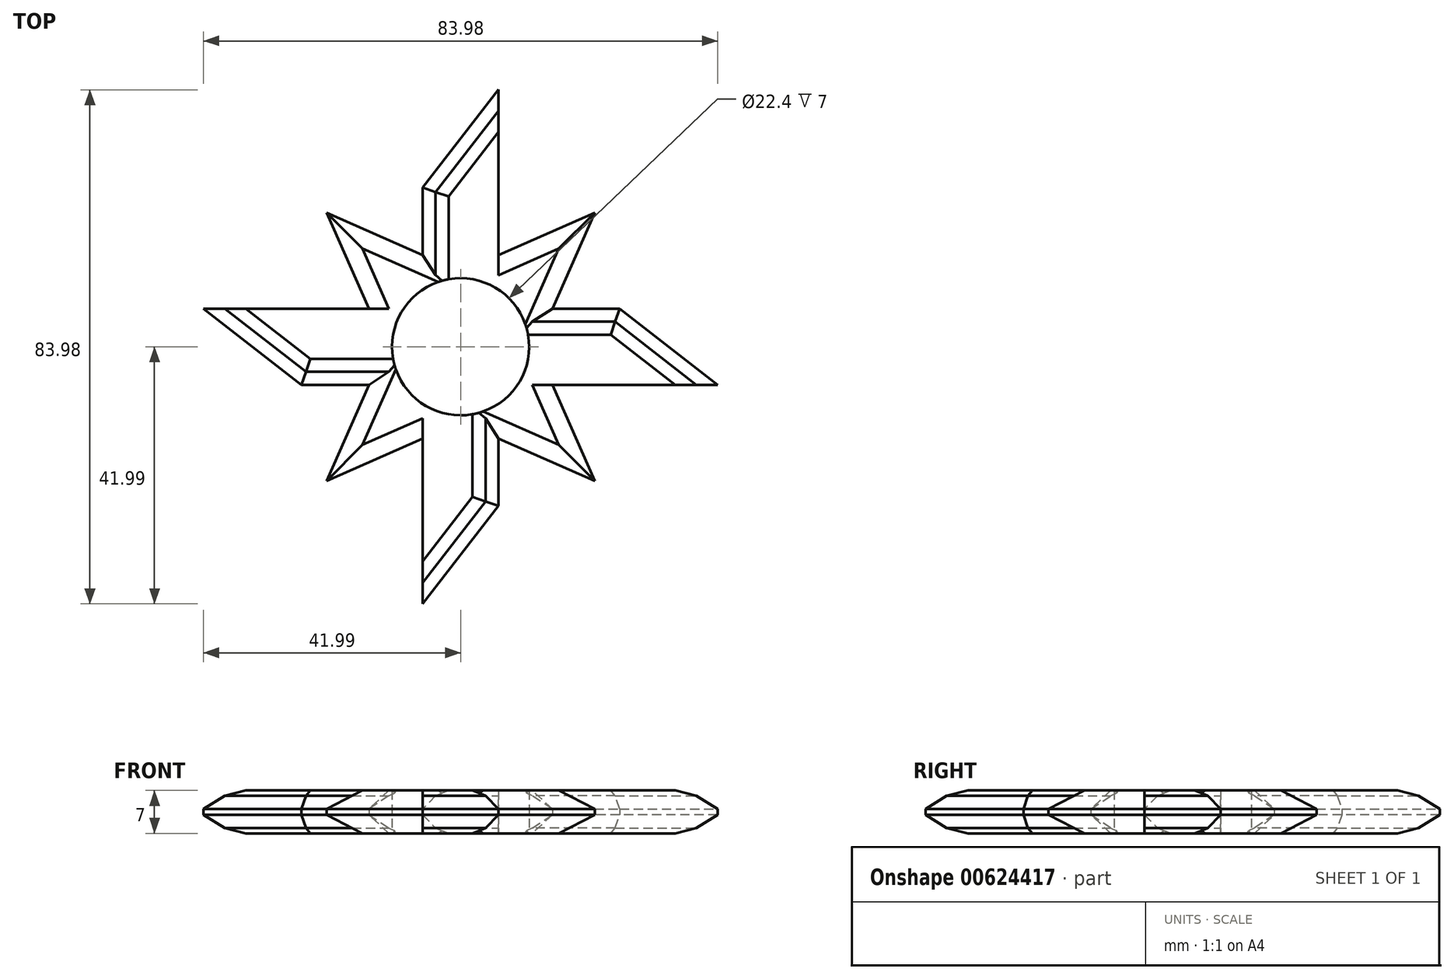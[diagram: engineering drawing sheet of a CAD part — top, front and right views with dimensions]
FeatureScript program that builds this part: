
annotation { "Feature Type Name" : "Feature", "Feature Type Description" : "" }
export const myFeature = defineFeature(function(context is Context, id is Id, definition is map)
    precondition{}
    {
        {
            var Q0;
            Q0=qCreatedBy(makeId("Top.planeOp"),FACE);
            var sketch = newSketch(context, id + "F0", { "sketchPlane" : qUnion([Q0])});
            skCircle(sketch, "E0", {"center": v(0, 0) * mm, "radius": 11.2 * mm});
            skCircle(sketch, "E1.cCircle", {"center": v(0, 0) * mm, "radius": 14.98 * mm, "construction": true});
            skLineSegment(sketch, "E1.0", {"start": v(14.98, 6.2) * mm, "end": v(14.98, -6.2) * mm});
            skLineSegment(sketch, "E1.1", {"start": v(14.98, -6.2) * mm, "end": v(6.2, -14.98) * mm});
            skLineSegment(sketch, "E1.2", {"start": v(6.2, -14.98) * mm, "end": v(-6.2, -14.98) * mm});
            skLineSegment(sketch, "E1.3", {"start": v(-6.2, -14.98) * mm, "end": v(-14.98, -6.2) * mm});
            skLineSegment(sketch, "E1.4", {"start": v(-14.98, -6.2) * mm, "end": v(-14.98, 6.2) * mm});
            skLineSegment(sketch, "E1.5", {"start": v(-14.98, 6.2) * mm, "end": v(-6.2, 14.98) * mm});
            skLineSegment(sketch, "E1.6", {"start": v(-6.2, 14.98) * mm, "end": v(6.2, 14.98) * mm});
            skLineSegment(sketch, "E1.7", {"start": v(6.2, 14.98) * mm, "end": v(14.98, 6.2) * mm});
            skPoint(sketch, "E1.0.midPoint", {"position": v(14.98, 0) * mm});
            skLineSegment(sketch, "E2", {"start": v(-14.98, 6.2) * mm, "end": v(-26, 6.2) * mm});
            skLineSegment(sketch, "E3", {"start": v(-26, 6.2) * mm, "end": v(-14.98, -6.2) * mm});
            skLineSegment(sketch, "E4", {"start": v(-14.98, -6.2) * mm, "end": v(-26, -6.2) * mm});
            skLineSegment(sketch, "E5", {"start": v(-26, -6.2) * mm, "end": v(-26, 6.2) * mm});
            skLineSegment(sketch, "E6", {"start": v(6.2, 14.98) * mm, "end": v(6.2, 26) * mm});
            skLineSegment(sketch, "E7", {"start": v(6.2, 26) * mm, "end": v(-6.2, 14.98) * mm});
            skLineSegment(sketch, "E8", {"start": v(-6.2, 14.98) * mm, "end": v(-6.2, 26) * mm});
            skLineSegment(sketch, "E9", {"start": v(-6.2, 26) * mm, "end": v(6.2, 26) * mm});
            skLineSegment(sketch, "E10", {"start": v(14.98, -6.2) * mm, "end": v(26, -6.2) * mm});
            skLineSegment(sketch, "E11", {"start": v(14.98, 6.2) * mm, "end": v(26, 6.2) * mm});
            skLineSegment(sketch, "E12", {"start": v(26, 6.2) * mm, "end": v(26, -6.2) * mm});
            skLineSegment(sketch, "E13", {"start": v(14.98, 6.2) * mm, "end": v(26, -6.2) * mm});
            skLineSegment(sketch, "E14", {"start": v(-6.2, -14.98) * mm, "end": v(-6.2, -26) * mm});
            skLineSegment(sketch, "E15", {"start": v(-6.2, -26) * mm, "end": v(6.2, -14.98) * mm});
            skLineSegment(sketch, "E16", {"start": v(6.2, -14.98) * mm, "end": v(6.2, -26) * mm});
            skLineSegment(sketch, "E17", {"start": v(6.2, -26) * mm, "end": v(-6.2, -26) * mm});
            skLineSegment(sketch, "E18", {"start": v(-14.98, 0) * mm, "end": v(0, 0) * mm});
            skLineSegment(sketch, "E19", {"start": v(-6.2, -26) * mm, "end": v(-6.2, -42) * mm});
            skLineSegment(sketch, "E20", {"start": v(-6.2, -42) * mm, "end": v(6.2, -26) * mm});
            skLineSegment(sketch, "E21", {"start": v(26, -6.2) * mm, "end": v(42, -6.2) * mm});
            skLineSegment(sketch, "E22", {"start": v(42, -6.2) * mm, "end": v(26, 6.2) * mm});
            skLineSegment(sketch, "E23", {"start": v(6.2, 26) * mm, "end": v(6.2, 42) * mm});
            skLineSegment(sketch, "E24", {"start": v(6.2, 42) * mm, "end": v(-6.2, 26) * mm});
            skLineSegment(sketch, "E25", {"start": v(-26, 6.2) * mm, "end": v(-42, 6.2) * mm});
            skLineSegment(sketch, "E26", {"start": v(-42, 6.2) * mm, "end": v(-26, -6.2) * mm});
            skLineSegment(sketch, "E27", {"start": v(10.6, -10.6) * mm, "end": v(21.9, -21.9) * mm});
            skLineSegment(sketch, "E28", {"start": v(21.9, -21.9) * mm, "end": v(6.2, -14.98) * mm});
            skLineSegment(sketch, "E29", {"start": v(14.98, -6.2) * mm, "end": v(21.9, -21.9) * mm});
            skLineSegment(sketch, "E30", {"start": v(-10.6, -10.6) * mm, "end": v(-21.9, -21.9) * mm});
            skLineSegment(sketch, "E31", {"start": v(-21.9, -21.9) * mm, "end": v(-6.2, -14.98) * mm});
            skLineSegment(sketch, "E32", {"start": v(-21.9, -21.9) * mm, "end": v(-14.98, -6.2) * mm});
            skLineSegment(sketch, "E33", {"start": v(-10.6, 10.6) * mm, "end": v(-21.9, 21.9) * mm});
            skLineSegment(sketch, "E34", {"start": v(-21.9, 21.9) * mm, "end": v(-14.98, 6.2) * mm});
            skLineSegment(sketch, "E35", {"start": v(-21.9, 21.9) * mm, "end": v(-6.2, 14.98) * mm});
            skLineSegment(sketch, "E36", {"start": v(10.6, 10.6) * mm, "end": v(21.9, 21.9) * mm});
            skLineSegment(sketch, "E37", {"start": v(21.9, 21.9) * mm, "end": v(6.2, 14.98) * mm});
            skLineSegment(sketch, "E38", {"start": v(21.9, 21.9) * mm, "end": v(14.98, 6.2) * mm});
            skSolve(sketch);
        }
        {
            var Q0;
            Q0=makeQuery(id+"F0.imprint","IMPRINT",FACE,{"disambiguationData":[TD([[makeQuery(id+"F0.imprint","IMPRINT",EDGE,{"derivedFrom":sQuery(id+"F0.wireOp",EDGE,"E9")}),1.0]])]});
            var Q1;
            Q1=makeQuery(id+"F0.imprint","IMPRINT",FACE,{"disambiguationData":[TD([[makeQuery(id+"F0.imprint","IMPRINT",EDGE,{"derivedFrom":sQuery(id+"F0.wireOp",EDGE,"E7")}),-1.0]])]});
            var Q2;
            Q2=makeQuery(id+"F0.imprint","IMPRINT",FACE,{"disambiguationData":[TD([[makeQuery(id+"F0.imprint","IMPRINT",EDGE,{"derivedFrom":sQuery(id+"F0.wireOp",EDGE,"E1.6")}),1.0]])]});
            var Q3;
            {var subQ2=sQuery(id+"F0.wireOp",EDGE,"E36");Q3=makeQuery(id+"F0.imprint","IMPRINT",FACE,{"disambiguationData":[TD([[makeQuery(id+"F0.imprint","IMPRINT",EDGE,{"derivedFrom":subQ2}),1.0]])]});}
            var Q4;
            {var subQ2=sQuery(id+"F0.wireOp",EDGE,"E36");Q4=makeQuery(id+"F0.imprint","IMPRINT",FACE,{"disambiguationData":[TD([[makeQuery(id+"F0.imprint","IMPRINT",EDGE,{"derivedFrom":subQ2}),-1.0]])]});}
            var Q5;
            Q5=makeQuery(id+"F0.imprint","IMPRINT",FACE,{"disambiguationData":[TD([[makeQuery(id+"F0.imprint","IMPRINT",EDGE,{"derivedFrom":sQuery(id+"F0.wireOp",EDGE,"E11")}),-1.0]])]});
            var Q6;
            Q6=makeQuery(id+"F0.imprint","IMPRINT",FACE,{"disambiguationData":[TD([[makeQuery(id+"F0.imprint","IMPRINT",EDGE,{"derivedFrom":sQuery(id+"F0.wireOp",EDGE,"E1.0")}),1.0]])]});
            var Q7;
            Q7=makeQuery(id+"F0.imprint","IMPRINT",FACE,{"disambiguationData":[TD([[makeQuery(id+"F0.imprint","IMPRINT",EDGE,{"derivedFrom":sQuery(id+"F0.wireOp",EDGE,"E12")}),1.0]])]});
            var Q8;
            {var subQ2=sQuery(id+"F0.wireOp",EDGE,"E27");Q8=makeQuery(id+"F0.imprint","IMPRINT",FACE,{"disambiguationData":[TD([[makeQuery(id+"F0.imprint","IMPRINT",EDGE,{"derivedFrom":subQ2}),-1.0]])]});}
            var Q9;
            Q9=makeQuery(id+"F0.imprint","IMPRINT",FACE,{"disambiguationData":[TD([[makeQuery(id+"F0.imprint","IMPRINT",EDGE,{"derivedFrom":sQuery(id+"F0.wireOp",EDGE,"E0")}),-1.0]])]});
            var Q10;
            Q10=makeQuery(id+"F0.imprint","IMPRINT",FACE,{"disambiguationData":[TD([[makeQuery(id+"F0.imprint","IMPRINT",EDGE,{"derivedFrom":sQuery(id+"F0.wireOp",EDGE,"E5")}),1.0]])]});
            var Q11;
            Q11=makeQuery(id+"F0.imprint","IMPRINT",FACE,{"disambiguationData":[TD([[makeQuery(id+"F0.imprint","IMPRINT",EDGE,{"derivedFrom":sQuery(id+"F0.wireOp",EDGE,"E3")}),-1.0]])]});
            var Q12;
            {var subQ3=sQuery(id+"F0.wireOp",EDGE,"E2");Q12=makeQuery(id+"F0.imprint","IMPRINT",FACE,{"disambiguationData":[TD([[makeQuery(id+"F0.imprint","IMPRINT",EDGE,{"derivedFrom":subQ3}),1.0]])]});}
            var Q13;
            {var subQ2=sQuery(id+"F0.wireOp",EDGE,"E33");Q13=makeQuery(id+"F0.imprint","IMPRINT",FACE,{"disambiguationData":[TD([[makeQuery(id+"F0.imprint","IMPRINT",EDGE,{"derivedFrom":subQ2}),1.0]])]});}
            var Q14;
            {var subQ2=sQuery(id+"F0.wireOp",EDGE,"E33");Q14=makeQuery(id+"F0.imprint","IMPRINT",FACE,{"disambiguationData":[TD([[makeQuery(id+"F0.imprint","IMPRINT",EDGE,{"derivedFrom":subQ2}),-1.0]])]});}
            var Q15;
            Q15=makeQuery(id+"F0.imprint","IMPRINT",FACE,{"disambiguationData":[TD([[makeQuery(id+"F0.imprint","IMPRINT",EDGE,{"derivedFrom":sQuery(id+"F0.wireOp",EDGE,"E15")}),-1.0]])]});
            var Q16;
            Q16=makeQuery(id+"F0.imprint","IMPRINT",FACE,{"disambiguationData":[TD([[makeQuery(id+"F0.imprint","IMPRINT",EDGE,{"derivedFrom":sQuery(id+"F0.wireOp",EDGE,"E17")}),1.0]])]});
            var Q17;
            Q17=makeQuery(id+"F0.imprint","IMPRINT",FACE,{"disambiguationData":[TD([[makeQuery(id+"F0.imprint","IMPRINT",EDGE,{"derivedFrom":sQuery(id+"F0.wireOp",EDGE,"E1.2")}),1.0]])]});
            var Q18;
            {var subQ2=sQuery(id+"F0.wireOp",EDGE,"E30");Q18=makeQuery(id+"F0.imprint","IMPRINT",FACE,{"disambiguationData":[TD([[makeQuery(id+"F0.imprint","IMPRINT",EDGE,{"derivedFrom":subQ2}),1.0]])]});}
            var Q19;
            {var subQ2=sQuery(id+"F0.wireOp",EDGE,"E30");Q19=makeQuery(id+"F0.imprint","IMPRINT",FACE,{"disambiguationData":[TD([[makeQuery(id+"F0.imprint","IMPRINT",EDGE,{"derivedFrom":subQ2}),-1.0]])]});}
            var Q20;
            {var subQ2=sQuery(id+"F0.wireOp",EDGE,"E27");Q20=makeQuery(id+"F0.imprint","IMPRINT",FACE,{"disambiguationData":[TD([[makeQuery(id+"F0.imprint","IMPRINT",EDGE,{"derivedFrom":subQ2}),1.0]])]});}
            extrude(context, id + "F1", {"entities" : qUnion([Q0, Q1, Q2, Q3, Q4, Q5, Q6, Q7, Q8, Q9, Q10, Q11, Q12, Q13, Q14, Q15, Q16, Q17, Q18, Q19, Q20]), "depth" : 7 * mm, "offsetDistance" : 25 * mm});
        }
        {
            var Q0;
            Q0=makeQuery(id+"F1.opExtrude","CAP_EDGE",EDGE,{"disambiguationData":[OSD([sQuery(id+"F0.wireOp",EDGE,"E24")])],"isStart":false});
            var Q1;
            Q1=makeQuery(id+"F1.opExtrude","CAP_EDGE",EDGE,{"disambiguationData":[OSD([sQuery(id+"F0.wireOp",EDGE,"E26")])],"isStart":false});
            var Q2;
            Q2=makeQuery(id+"F1.opExtrude","CAP_EDGE",EDGE,{"disambiguationData":[OSD([sQuery(id+"F0.wireOp",EDGE,"E20")])],"isStart":false});
            var Q3;
            Q3=makeQuery(id+"F1.opExtrude","CAP_EDGE",EDGE,{"disambiguationData":[OSD([sQuery(id+"F0.wireOp",EDGE,"E22")])],"isStart":false});
            var Q4;
            Q4=makeQuery(id+"F1.opExtrude","CAP_EDGE",EDGE,{"disambiguationData":[OSD([sQuery(id+"F0.wireOp",EDGE,"E11")])],"isStart":false});
            var Q5;
            Q5=makeQuery(id+"F1.opExtrude","CAP_EDGE",EDGE,{"disambiguationData":[OSD([sQuery(id+"F0.wireOp",EDGE,"E16")])],"isStart":false});
            var Q6;
            Q6=makeQuery(id+"F1.opExtrude","CAP_EDGE",EDGE,{"disambiguationData":[OSD([sQuery(id+"F0.wireOp",EDGE,"E4")])],"isStart":false});
            var Q7;
            Q7=makeQuery(id+"F1.opExtrude","CAP_EDGE",EDGE,{"disambiguationData":[OSD([sQuery(id+"F0.wireOp",EDGE,"E8")])],"isStart":false});
            var Q8;
            Q8=makeQuery(id+"F1.opExtrude","CAP_EDGE",EDGE,{"disambiguationData":[OSD([sQuery(id+"F0.wireOp",EDGE,"E35")])],"isStart":false});
            var Q9;
            Q9=makeQuery(id+"F1.opExtrude","CAP_EDGE",EDGE,{"disambiguationData":[OSD([sQuery(id+"F0.wireOp",EDGE,"E34")])],"isStart":false});
            var Q10;
            Q10=makeQuery(id+"F1.opExtrude","CAP_EDGE",EDGE,{"disambiguationData":[OSD([sQuery(id+"F0.wireOp",EDGE,"E37")])],"isStart":false});
            var Q11;
            Q11=makeQuery(id+"F1.opExtrude","CAP_EDGE",EDGE,{"disambiguationData":[OSD([sQuery(id+"F0.wireOp",EDGE,"E38")])],"isStart":false});
            var Q12;
            Q12=makeQuery(id+"F1.opExtrude","CAP_EDGE",EDGE,{"disambiguationData":[OSD([sQuery(id+"F0.wireOp",EDGE,"E32")])],"isStart":false});
            var Q13;
            Q13=makeQuery(id+"F1.opExtrude","CAP_EDGE",EDGE,{"disambiguationData":[OSD([sQuery(id+"F0.wireOp",EDGE,"E31")])],"isStart":false});
            var Q14;
            Q14=makeQuery(id+"F1.opExtrude","CAP_EDGE",EDGE,{"disambiguationData":[OSD([sQuery(id+"F0.wireOp",EDGE,"E28")])],"isStart":false});
            var Q15;
            Q15=makeQuery(id+"F1.opExtrude","CAP_EDGE",EDGE,{"disambiguationData":[OSD([sQuery(id+"F0.wireOp",EDGE,"E29")])],"isStart":false});
            var Q16;
            Q16=makeQuery(id+"F1.opExtrude","CAP_EDGE",EDGE,{"disambiguationData":[OSD([sQuery(id+"F0.wireOp",EDGE,"E22")])],"isStart":true});
            var Q17;
            Q17=makeQuery(id+"F1.opExtrude","CAP_EDGE",EDGE,{"disambiguationData":[OSD([sQuery(id+"F0.wireOp",EDGE,"E11")])],"isStart":true});
            var Q18;
            Q18=makeQuery(id+"F1.opExtrude","CAP_EDGE",EDGE,{"disambiguationData":[OSD([sQuery(id+"F0.wireOp",EDGE,"E38")])],"isStart":true});
            var Q19;
            Q19=makeQuery(id+"F1.opExtrude","CAP_EDGE",EDGE,{"disambiguationData":[OSD([sQuery(id+"F0.wireOp",EDGE,"E37")])],"isStart":true});
            var Q20;
            Q20=makeQuery(id+"F1.opExtrude","CAP_EDGE",EDGE,{"disambiguationData":[OSD([sQuery(id+"F0.wireOp",EDGE,"E24")])],"isStart":true});
            var Q21;
            Q21=makeQuery(id+"F1.opExtrude","CAP_EDGE",EDGE,{"disambiguationData":[OSD([sQuery(id+"F0.wireOp",EDGE,"E8")])],"isStart":true});
            var Q22;
            Q22=makeQuery(id+"F1.opExtrude","CAP_EDGE",EDGE,{"disambiguationData":[OSD([sQuery(id+"F0.wireOp",EDGE,"E35")])],"isStart":true});
            var Q23;
            Q23=makeQuery(id+"F1.opExtrude","CAP_EDGE",EDGE,{"disambiguationData":[OSD([sQuery(id+"F0.wireOp",EDGE,"E34")])],"isStart":true});
            var Q24;
            Q24=makeQuery(id+"F1.opExtrude","CAP_EDGE",EDGE,{"disambiguationData":[OSD([sQuery(id+"F0.wireOp",EDGE,"E26")])],"isStart":true});
            var Q25;
            Q25=makeQuery(id+"F1.opExtrude","CAP_EDGE",EDGE,{"disambiguationData":[OSD([sQuery(id+"F0.wireOp",EDGE,"E4")])],"isStart":true});
            var Q26;
            Q26=makeQuery(id+"F1.opExtrude","CAP_EDGE",EDGE,{"disambiguationData":[OSD([sQuery(id+"F0.wireOp",EDGE,"E32")])],"isStart":true});
            var Q27;
            Q27=makeQuery(id+"F1.opExtrude","CAP_EDGE",EDGE,{"disambiguationData":[OSD([sQuery(id+"F0.wireOp",EDGE,"E31")])],"isStart":true});
            var Q28;
            Q28=makeQuery(id+"F1.opExtrude","CAP_EDGE",EDGE,{"disambiguationData":[OSD([sQuery(id+"F0.wireOp",EDGE,"E16")])],"isStart":true});
            var Q29;
            Q29=makeQuery(id+"F1.opExtrude","CAP_EDGE",EDGE,{"disambiguationData":[OSD([sQuery(id+"F0.wireOp",EDGE,"E20")])],"isStart":true});
            var Q30;
            Q30=makeQuery(id+"F1.opExtrude","CAP_EDGE",EDGE,{"disambiguationData":[OSD([sQuery(id+"F0.wireOp",EDGE,"E29")])],"isStart":true});
            var Q31;
            Q31=makeQuery(id+"F1.opExtrude","CAP_EDGE",EDGE,{"disambiguationData":[OSD([sQuery(id+"F0.wireOp",EDGE,"E28")])],"isStart":true});
            chamfer(context, id + "F2", {"entities" : qUnion([Q0, Q1, Q2, Q3, Q4, Q5, Q6, Q7, Q8, Q9, Q10, Q11, Q12, Q13, Q14, Q15, Q16, Q17, Q18, Q19, Q20, Q21, Q22, Q23, Q24, Q25, Q26, Q27, Q28, Q29, Q30, Q31]), "width" : 3 * mm, "tangentPropagation" : true});
        }
        {
            var Q0;
            {var subQ0=sQuery(id+"F0.wireOp",EDGE,"E20");Q0=makeQuery(id+"F2.opChamfer","BLEND_EDGE",EDGE,{"blendedFrom":[makeQuery(id+"F1.opExtrude","CAP_EDGE",EDGE,{"disambiguationData":[OSD([subQ0])],"isStart":true}),makeQuery(id+"F1.opExtrude","CAP_FACE",FACE,{"disambiguationData":[OSD([sQuery(id+"F0.wireOp",EDGE,"E0"),sQuery(id+"F0.wireOp",EDGE,"E2"),sQuery(id+"F0.wireOp",EDGE,"E4"),sQuery(id+"F0.wireOp",EDGE,"E6"),sQuery(id+"F0.wireOp",EDGE,"E8"),sQuery(id+"F0.wireOp",EDGE,"E10"),sQuery(id+"F0.wireOp",EDGE,"E11"),sQuery(id+"F0.wireOp",EDGE,"E14"),sQuery(id+"F0.wireOp",EDGE,"E16"),sQuery(id+"F0.wireOp",EDGE,"E19"),subQ0,sQuery(id+"F0.wireOp",EDGE,"E21"),sQuery(id+"F0.wireOp",EDGE,"E22"),sQuery(id+"F0.wireOp",EDGE,"E23"),sQuery(id+"F0.wireOp",EDGE,"E24"),sQuery(id+"F0.wireOp",EDGE,"E25"),sQuery(id+"F0.wireOp",EDGE,"E26"),sQuery(id+"F0.wireOp",EDGE,"E28"),sQuery(id+"F0.wireOp",EDGE,"E29"),sQuery(id+"F0.wireOp",EDGE,"E31"),sQuery(id+"F0.wireOp",EDGE,"E32"),sQuery(id+"F0.wireOp",EDGE,"E34"),sQuery(id+"F0.wireOp",EDGE,"E35"),sQuery(id+"F0.wireOp",EDGE,"E37"),sQuery(id+"F0.wireOp",EDGE,"E38")])],"isStart":true})],"blendedInto":[makeQuery(id+"F1.opExtrude","CAP_FACE",FACE,{"disambiguationData":[OSD([sQuery(id+"F0.wireOp",EDGE,"E0"),sQuery(id+"F0.wireOp",EDGE,"E2"),sQuery(id+"F0.wireOp",EDGE,"E4"),sQuery(id+"F0.wireOp",EDGE,"E6"),sQuery(id+"F0.wireOp",EDGE,"E8"),sQuery(id+"F0.wireOp",EDGE,"E10"),sQuery(id+"F0.wireOp",EDGE,"E11"),sQuery(id+"F0.wireOp",EDGE,"E14"),sQuery(id+"F0.wireOp",EDGE,"E16"),sQuery(id+"F0.wireOp",EDGE,"E19"),subQ0,sQuery(id+"F0.wireOp",EDGE,"E21"),sQuery(id+"F0.wireOp",EDGE,"E22"),sQuery(id+"F0.wireOp",EDGE,"E23"),sQuery(id+"F0.wireOp",EDGE,"E24"),sQuery(id+"F0.wireOp",EDGE,"E25"),sQuery(id+"F0.wireOp",EDGE,"E26"),sQuery(id+"F0.wireOp",EDGE,"E28"),sQuery(id+"F0.wireOp",EDGE,"E29"),sQuery(id+"F0.wireOp",EDGE,"E31"),sQuery(id+"F0.wireOp",EDGE,"E32"),sQuery(id+"F0.wireOp",EDGE,"E34"),sQuery(id+"F0.wireOp",EDGE,"E35"),sQuery(id+"F0.wireOp",EDGE,"E37"),sQuery(id+"F0.wireOp",EDGE,"E38")])],"isStart":true})]});}
            var Q1;
            {var subQ0=sQuery(id+"F0.wireOp",EDGE,"E16");Q1=makeQuery(id+"F2.opChamfer","BLEND_EDGE",EDGE,{"blendedFrom":[makeQuery(id+"F1.opExtrude","CAP_EDGE",EDGE,{"disambiguationData":[OSD([subQ0])],"isStart":true}),makeQuery(id+"F1.opExtrude","CAP_FACE",FACE,{"disambiguationData":[OSD([sQuery(id+"F0.wireOp",EDGE,"E0"),sQuery(id+"F0.wireOp",EDGE,"E2"),sQuery(id+"F0.wireOp",EDGE,"E4"),sQuery(id+"F0.wireOp",EDGE,"E6"),sQuery(id+"F0.wireOp",EDGE,"E8"),sQuery(id+"F0.wireOp",EDGE,"E10"),sQuery(id+"F0.wireOp",EDGE,"E11"),sQuery(id+"F0.wireOp",EDGE,"E14"),subQ0,sQuery(id+"F0.wireOp",EDGE,"E19"),sQuery(id+"F0.wireOp",EDGE,"E20"),sQuery(id+"F0.wireOp",EDGE,"E21"),sQuery(id+"F0.wireOp",EDGE,"E22"),sQuery(id+"F0.wireOp",EDGE,"E23"),sQuery(id+"F0.wireOp",EDGE,"E24"),sQuery(id+"F0.wireOp",EDGE,"E25"),sQuery(id+"F0.wireOp",EDGE,"E26"),sQuery(id+"F0.wireOp",EDGE,"E28"),sQuery(id+"F0.wireOp",EDGE,"E29"),sQuery(id+"F0.wireOp",EDGE,"E31"),sQuery(id+"F0.wireOp",EDGE,"E32"),sQuery(id+"F0.wireOp",EDGE,"E34"),sQuery(id+"F0.wireOp",EDGE,"E35"),sQuery(id+"F0.wireOp",EDGE,"E37"),sQuery(id+"F0.wireOp",EDGE,"E38")])],"isStart":true})],"blendedInto":[makeQuery(id+"F1.opExtrude","CAP_FACE",FACE,{"disambiguationData":[OSD([sQuery(id+"F0.wireOp",EDGE,"E0"),sQuery(id+"F0.wireOp",EDGE,"E2"),sQuery(id+"F0.wireOp",EDGE,"E4"),sQuery(id+"F0.wireOp",EDGE,"E6"),sQuery(id+"F0.wireOp",EDGE,"E8"),sQuery(id+"F0.wireOp",EDGE,"E10"),sQuery(id+"F0.wireOp",EDGE,"E11"),sQuery(id+"F0.wireOp",EDGE,"E14"),subQ0,sQuery(id+"F0.wireOp",EDGE,"E19"),sQuery(id+"F0.wireOp",EDGE,"E20"),sQuery(id+"F0.wireOp",EDGE,"E21"),sQuery(id+"F0.wireOp",EDGE,"E22"),sQuery(id+"F0.wireOp",EDGE,"E23"),sQuery(id+"F0.wireOp",EDGE,"E24"),sQuery(id+"F0.wireOp",EDGE,"E25"),sQuery(id+"F0.wireOp",EDGE,"E26"),sQuery(id+"F0.wireOp",EDGE,"E28"),sQuery(id+"F0.wireOp",EDGE,"E29"),sQuery(id+"F0.wireOp",EDGE,"E31"),sQuery(id+"F0.wireOp",EDGE,"E32"),sQuery(id+"F0.wireOp",EDGE,"E34"),sQuery(id+"F0.wireOp",EDGE,"E35"),sQuery(id+"F0.wireOp",EDGE,"E37"),sQuery(id+"F0.wireOp",EDGE,"E38")])],"isStart":true})]});}
            var Q2;
            {var subQ0=sQuery(id+"F0.wireOp",EDGE,"E26");Q2=makeQuery(id+"F2.opChamfer","BLEND_EDGE",EDGE,{"blendedFrom":[makeQuery(id+"F1.opExtrude","CAP_EDGE",EDGE,{"disambiguationData":[OSD([subQ0])],"isStart":true}),makeQuery(id+"F1.opExtrude","CAP_FACE",FACE,{"disambiguationData":[OSD([sQuery(id+"F0.wireOp",EDGE,"E0"),sQuery(id+"F0.wireOp",EDGE,"E2"),sQuery(id+"F0.wireOp",EDGE,"E4"),sQuery(id+"F0.wireOp",EDGE,"E6"),sQuery(id+"F0.wireOp",EDGE,"E8"),sQuery(id+"F0.wireOp",EDGE,"E10"),sQuery(id+"F0.wireOp",EDGE,"E11"),sQuery(id+"F0.wireOp",EDGE,"E14"),sQuery(id+"F0.wireOp",EDGE,"E16"),sQuery(id+"F0.wireOp",EDGE,"E19"),sQuery(id+"F0.wireOp",EDGE,"E20"),sQuery(id+"F0.wireOp",EDGE,"E21"),sQuery(id+"F0.wireOp",EDGE,"E22"),sQuery(id+"F0.wireOp",EDGE,"E23"),sQuery(id+"F0.wireOp",EDGE,"E24"),sQuery(id+"F0.wireOp",EDGE,"E25"),subQ0,sQuery(id+"F0.wireOp",EDGE,"E28"),sQuery(id+"F0.wireOp",EDGE,"E29"),sQuery(id+"F0.wireOp",EDGE,"E31"),sQuery(id+"F0.wireOp",EDGE,"E32"),sQuery(id+"F0.wireOp",EDGE,"E34"),sQuery(id+"F0.wireOp",EDGE,"E35"),sQuery(id+"F0.wireOp",EDGE,"E37"),sQuery(id+"F0.wireOp",EDGE,"E38")])],"isStart":true})],"blendedInto":[makeQuery(id+"F1.opExtrude","CAP_FACE",FACE,{"disambiguationData":[OSD([sQuery(id+"F0.wireOp",EDGE,"E0"),sQuery(id+"F0.wireOp",EDGE,"E2"),sQuery(id+"F0.wireOp",EDGE,"E4"),sQuery(id+"F0.wireOp",EDGE,"E6"),sQuery(id+"F0.wireOp",EDGE,"E8"),sQuery(id+"F0.wireOp",EDGE,"E10"),sQuery(id+"F0.wireOp",EDGE,"E11"),sQuery(id+"F0.wireOp",EDGE,"E14"),sQuery(id+"F0.wireOp",EDGE,"E16"),sQuery(id+"F0.wireOp",EDGE,"E19"),sQuery(id+"F0.wireOp",EDGE,"E20"),sQuery(id+"F0.wireOp",EDGE,"E21"),sQuery(id+"F0.wireOp",EDGE,"E22"),sQuery(id+"F0.wireOp",EDGE,"E23"),sQuery(id+"F0.wireOp",EDGE,"E24"),sQuery(id+"F0.wireOp",EDGE,"E25"),subQ0,sQuery(id+"F0.wireOp",EDGE,"E28"),sQuery(id+"F0.wireOp",EDGE,"E29"),sQuery(id+"F0.wireOp",EDGE,"E31"),sQuery(id+"F0.wireOp",EDGE,"E32"),sQuery(id+"F0.wireOp",EDGE,"E34"),sQuery(id+"F0.wireOp",EDGE,"E35"),sQuery(id+"F0.wireOp",EDGE,"E37"),sQuery(id+"F0.wireOp",EDGE,"E38")])],"isStart":true})]});}
            var Q3;
            {var subQ0=sQuery(id+"F0.wireOp",EDGE,"E4");Q3=makeQuery(id+"F2.opChamfer","BLEND_EDGE",EDGE,{"blendedFrom":[makeQuery(id+"F1.opExtrude","CAP_EDGE",EDGE,{"disambiguationData":[OSD([subQ0])],"isStart":true}),makeQuery(id+"F1.opExtrude","CAP_FACE",FACE,{"disambiguationData":[OSD([sQuery(id+"F0.wireOp",EDGE,"E0"),sQuery(id+"F0.wireOp",EDGE,"E2"),subQ0,sQuery(id+"F0.wireOp",EDGE,"E6"),sQuery(id+"F0.wireOp",EDGE,"E8"),sQuery(id+"F0.wireOp",EDGE,"E10"),sQuery(id+"F0.wireOp",EDGE,"E11"),sQuery(id+"F0.wireOp",EDGE,"E14"),sQuery(id+"F0.wireOp",EDGE,"E16"),sQuery(id+"F0.wireOp",EDGE,"E19"),sQuery(id+"F0.wireOp",EDGE,"E20"),sQuery(id+"F0.wireOp",EDGE,"E21"),sQuery(id+"F0.wireOp",EDGE,"E22"),sQuery(id+"F0.wireOp",EDGE,"E23"),sQuery(id+"F0.wireOp",EDGE,"E24"),sQuery(id+"F0.wireOp",EDGE,"E25"),sQuery(id+"F0.wireOp",EDGE,"E26"),sQuery(id+"F0.wireOp",EDGE,"E28"),sQuery(id+"F0.wireOp",EDGE,"E29"),sQuery(id+"F0.wireOp",EDGE,"E31"),sQuery(id+"F0.wireOp",EDGE,"E32"),sQuery(id+"F0.wireOp",EDGE,"E34"),sQuery(id+"F0.wireOp",EDGE,"E35"),sQuery(id+"F0.wireOp",EDGE,"E37"),sQuery(id+"F0.wireOp",EDGE,"E38")])],"isStart":true})],"blendedInto":[makeQuery(id+"F1.opExtrude","CAP_FACE",FACE,{"disambiguationData":[OSD([sQuery(id+"F0.wireOp",EDGE,"E0"),sQuery(id+"F0.wireOp",EDGE,"E2"),subQ0,sQuery(id+"F0.wireOp",EDGE,"E6"),sQuery(id+"F0.wireOp",EDGE,"E8"),sQuery(id+"F0.wireOp",EDGE,"E10"),sQuery(id+"F0.wireOp",EDGE,"E11"),sQuery(id+"F0.wireOp",EDGE,"E14"),sQuery(id+"F0.wireOp",EDGE,"E16"),sQuery(id+"F0.wireOp",EDGE,"E19"),sQuery(id+"F0.wireOp",EDGE,"E20"),sQuery(id+"F0.wireOp",EDGE,"E21"),sQuery(id+"F0.wireOp",EDGE,"E22"),sQuery(id+"F0.wireOp",EDGE,"E23"),sQuery(id+"F0.wireOp",EDGE,"E24"),sQuery(id+"F0.wireOp",EDGE,"E25"),sQuery(id+"F0.wireOp",EDGE,"E26"),sQuery(id+"F0.wireOp",EDGE,"E28"),sQuery(id+"F0.wireOp",EDGE,"E29"),sQuery(id+"F0.wireOp",EDGE,"E31"),sQuery(id+"F0.wireOp",EDGE,"E32"),sQuery(id+"F0.wireOp",EDGE,"E34"),sQuery(id+"F0.wireOp",EDGE,"E35"),sQuery(id+"F0.wireOp",EDGE,"E37"),sQuery(id+"F0.wireOp",EDGE,"E38")])],"isStart":true})]});}
            var Q4;
            {var subQ0=sQuery(id+"F0.wireOp",EDGE,"E8");Q4=makeQuery(id+"F2.opChamfer","BLEND_EDGE",EDGE,{"blendedFrom":[makeQuery(id+"F1.opExtrude","CAP_EDGE",EDGE,{"disambiguationData":[OSD([subQ0])],"isStart":true}),makeQuery(id+"F1.opExtrude","CAP_FACE",FACE,{"disambiguationData":[OSD([sQuery(id+"F0.wireOp",EDGE,"E0"),sQuery(id+"F0.wireOp",EDGE,"E2"),sQuery(id+"F0.wireOp",EDGE,"E4"),sQuery(id+"F0.wireOp",EDGE,"E6"),subQ0,sQuery(id+"F0.wireOp",EDGE,"E10"),sQuery(id+"F0.wireOp",EDGE,"E11"),sQuery(id+"F0.wireOp",EDGE,"E14"),sQuery(id+"F0.wireOp",EDGE,"E16"),sQuery(id+"F0.wireOp",EDGE,"E19"),sQuery(id+"F0.wireOp",EDGE,"E20"),sQuery(id+"F0.wireOp",EDGE,"E21"),sQuery(id+"F0.wireOp",EDGE,"E22"),sQuery(id+"F0.wireOp",EDGE,"E23"),sQuery(id+"F0.wireOp",EDGE,"E24"),sQuery(id+"F0.wireOp",EDGE,"E25"),sQuery(id+"F0.wireOp",EDGE,"E26"),sQuery(id+"F0.wireOp",EDGE,"E28"),sQuery(id+"F0.wireOp",EDGE,"E29"),sQuery(id+"F0.wireOp",EDGE,"E31"),sQuery(id+"F0.wireOp",EDGE,"E32"),sQuery(id+"F0.wireOp",EDGE,"E34"),sQuery(id+"F0.wireOp",EDGE,"E35"),sQuery(id+"F0.wireOp",EDGE,"E37"),sQuery(id+"F0.wireOp",EDGE,"E38")])],"isStart":true})],"blendedInto":[makeQuery(id+"F1.opExtrude","CAP_FACE",FACE,{"disambiguationData":[OSD([sQuery(id+"F0.wireOp",EDGE,"E0"),sQuery(id+"F0.wireOp",EDGE,"E2"),sQuery(id+"F0.wireOp",EDGE,"E4"),sQuery(id+"F0.wireOp",EDGE,"E6"),subQ0,sQuery(id+"F0.wireOp",EDGE,"E10"),sQuery(id+"F0.wireOp",EDGE,"E11"),sQuery(id+"F0.wireOp",EDGE,"E14"),sQuery(id+"F0.wireOp",EDGE,"E16"),sQuery(id+"F0.wireOp",EDGE,"E19"),sQuery(id+"F0.wireOp",EDGE,"E20"),sQuery(id+"F0.wireOp",EDGE,"E21"),sQuery(id+"F0.wireOp",EDGE,"E22"),sQuery(id+"F0.wireOp",EDGE,"E23"),sQuery(id+"F0.wireOp",EDGE,"E24"),sQuery(id+"F0.wireOp",EDGE,"E25"),sQuery(id+"F0.wireOp",EDGE,"E26"),sQuery(id+"F0.wireOp",EDGE,"E28"),sQuery(id+"F0.wireOp",EDGE,"E29"),sQuery(id+"F0.wireOp",EDGE,"E31"),sQuery(id+"F0.wireOp",EDGE,"E32"),sQuery(id+"F0.wireOp",EDGE,"E34"),sQuery(id+"F0.wireOp",EDGE,"E35"),sQuery(id+"F0.wireOp",EDGE,"E37"),sQuery(id+"F0.wireOp",EDGE,"E38")])],"isStart":true})]});}
            var Q5;
            {var subQ0=sQuery(id+"F0.wireOp",EDGE,"E24");Q5=makeQuery(id+"F2.opChamfer","BLEND_EDGE",EDGE,{"blendedFrom":[makeQuery(id+"F1.opExtrude","CAP_EDGE",EDGE,{"disambiguationData":[OSD([subQ0])],"isStart":true}),makeQuery(id+"F1.opExtrude","CAP_FACE",FACE,{"disambiguationData":[OSD([sQuery(id+"F0.wireOp",EDGE,"E0"),sQuery(id+"F0.wireOp",EDGE,"E2"),sQuery(id+"F0.wireOp",EDGE,"E4"),sQuery(id+"F0.wireOp",EDGE,"E6"),sQuery(id+"F0.wireOp",EDGE,"E8"),sQuery(id+"F0.wireOp",EDGE,"E10"),sQuery(id+"F0.wireOp",EDGE,"E11"),sQuery(id+"F0.wireOp",EDGE,"E14"),sQuery(id+"F0.wireOp",EDGE,"E16"),sQuery(id+"F0.wireOp",EDGE,"E19"),sQuery(id+"F0.wireOp",EDGE,"E20"),sQuery(id+"F0.wireOp",EDGE,"E21"),sQuery(id+"F0.wireOp",EDGE,"E22"),sQuery(id+"F0.wireOp",EDGE,"E23"),subQ0,sQuery(id+"F0.wireOp",EDGE,"E25"),sQuery(id+"F0.wireOp",EDGE,"E26"),sQuery(id+"F0.wireOp",EDGE,"E28"),sQuery(id+"F0.wireOp",EDGE,"E29"),sQuery(id+"F0.wireOp",EDGE,"E31"),sQuery(id+"F0.wireOp",EDGE,"E32"),sQuery(id+"F0.wireOp",EDGE,"E34"),sQuery(id+"F0.wireOp",EDGE,"E35"),sQuery(id+"F0.wireOp",EDGE,"E37"),sQuery(id+"F0.wireOp",EDGE,"E38")])],"isStart":true})],"blendedInto":[makeQuery(id+"F1.opExtrude","CAP_FACE",FACE,{"disambiguationData":[OSD([sQuery(id+"F0.wireOp",EDGE,"E0"),sQuery(id+"F0.wireOp",EDGE,"E2"),sQuery(id+"F0.wireOp",EDGE,"E4"),sQuery(id+"F0.wireOp",EDGE,"E6"),sQuery(id+"F0.wireOp",EDGE,"E8"),sQuery(id+"F0.wireOp",EDGE,"E10"),sQuery(id+"F0.wireOp",EDGE,"E11"),sQuery(id+"F0.wireOp",EDGE,"E14"),sQuery(id+"F0.wireOp",EDGE,"E16"),sQuery(id+"F0.wireOp",EDGE,"E19"),sQuery(id+"F0.wireOp",EDGE,"E20"),sQuery(id+"F0.wireOp",EDGE,"E21"),sQuery(id+"F0.wireOp",EDGE,"E22"),sQuery(id+"F0.wireOp",EDGE,"E23"),subQ0,sQuery(id+"F0.wireOp",EDGE,"E25"),sQuery(id+"F0.wireOp",EDGE,"E26"),sQuery(id+"F0.wireOp",EDGE,"E28"),sQuery(id+"F0.wireOp",EDGE,"E29"),sQuery(id+"F0.wireOp",EDGE,"E31"),sQuery(id+"F0.wireOp",EDGE,"E32"),sQuery(id+"F0.wireOp",EDGE,"E34"),sQuery(id+"F0.wireOp",EDGE,"E35"),sQuery(id+"F0.wireOp",EDGE,"E37"),sQuery(id+"F0.wireOp",EDGE,"E38")])],"isStart":true})]});}
            var Q6;
            {var subQ0=sQuery(id+"F0.wireOp",EDGE,"E11");Q6=makeQuery(id+"F2.opChamfer","BLEND_EDGE",EDGE,{"blendedFrom":[makeQuery(id+"F1.opExtrude","CAP_EDGE",EDGE,{"disambiguationData":[OSD([subQ0])],"isStart":true}),makeQuery(id+"F1.opExtrude","CAP_FACE",FACE,{"disambiguationData":[OSD([sQuery(id+"F0.wireOp",EDGE,"E0"),sQuery(id+"F0.wireOp",EDGE,"E2"),sQuery(id+"F0.wireOp",EDGE,"E4"),sQuery(id+"F0.wireOp",EDGE,"E6"),sQuery(id+"F0.wireOp",EDGE,"E8"),sQuery(id+"F0.wireOp",EDGE,"E10"),subQ0,sQuery(id+"F0.wireOp",EDGE,"E14"),sQuery(id+"F0.wireOp",EDGE,"E16"),sQuery(id+"F0.wireOp",EDGE,"E19"),sQuery(id+"F0.wireOp",EDGE,"E20"),sQuery(id+"F0.wireOp",EDGE,"E21"),sQuery(id+"F0.wireOp",EDGE,"E22"),sQuery(id+"F0.wireOp",EDGE,"E23"),sQuery(id+"F0.wireOp",EDGE,"E24"),sQuery(id+"F0.wireOp",EDGE,"E25"),sQuery(id+"F0.wireOp",EDGE,"E26"),sQuery(id+"F0.wireOp",EDGE,"E28"),sQuery(id+"F0.wireOp",EDGE,"E29"),sQuery(id+"F0.wireOp",EDGE,"E31"),sQuery(id+"F0.wireOp",EDGE,"E32"),sQuery(id+"F0.wireOp",EDGE,"E34"),sQuery(id+"F0.wireOp",EDGE,"E35"),sQuery(id+"F0.wireOp",EDGE,"E37"),sQuery(id+"F0.wireOp",EDGE,"E38")])],"isStart":true})],"blendedInto":[makeQuery(id+"F1.opExtrude","CAP_FACE",FACE,{"disambiguationData":[OSD([sQuery(id+"F0.wireOp",EDGE,"E0"),sQuery(id+"F0.wireOp",EDGE,"E2"),sQuery(id+"F0.wireOp",EDGE,"E4"),sQuery(id+"F0.wireOp",EDGE,"E6"),sQuery(id+"F0.wireOp",EDGE,"E8"),sQuery(id+"F0.wireOp",EDGE,"E10"),subQ0,sQuery(id+"F0.wireOp",EDGE,"E14"),sQuery(id+"F0.wireOp",EDGE,"E16"),sQuery(id+"F0.wireOp",EDGE,"E19"),sQuery(id+"F0.wireOp",EDGE,"E20"),sQuery(id+"F0.wireOp",EDGE,"E21"),sQuery(id+"F0.wireOp",EDGE,"E22"),sQuery(id+"F0.wireOp",EDGE,"E23"),sQuery(id+"F0.wireOp",EDGE,"E24"),sQuery(id+"F0.wireOp",EDGE,"E25"),sQuery(id+"F0.wireOp",EDGE,"E26"),sQuery(id+"F0.wireOp",EDGE,"E28"),sQuery(id+"F0.wireOp",EDGE,"E29"),sQuery(id+"F0.wireOp",EDGE,"E31"),sQuery(id+"F0.wireOp",EDGE,"E32"),sQuery(id+"F0.wireOp",EDGE,"E34"),sQuery(id+"F0.wireOp",EDGE,"E35"),sQuery(id+"F0.wireOp",EDGE,"E37"),sQuery(id+"F0.wireOp",EDGE,"E38")])],"isStart":true})]});}
            var Q7;
            {var subQ0=sQuery(id+"F0.wireOp",EDGE,"E22");Q7=makeQuery(id+"F2.opChamfer","BLEND_EDGE",EDGE,{"blendedFrom":[makeQuery(id+"F1.opExtrude","CAP_EDGE",EDGE,{"disambiguationData":[OSD([subQ0])],"isStart":true}),makeQuery(id+"F1.opExtrude","CAP_FACE",FACE,{"disambiguationData":[OSD([sQuery(id+"F0.wireOp",EDGE,"E0"),sQuery(id+"F0.wireOp",EDGE,"E2"),sQuery(id+"F0.wireOp",EDGE,"E4"),sQuery(id+"F0.wireOp",EDGE,"E6"),sQuery(id+"F0.wireOp",EDGE,"E8"),sQuery(id+"F0.wireOp",EDGE,"E10"),sQuery(id+"F0.wireOp",EDGE,"E11"),sQuery(id+"F0.wireOp",EDGE,"E14"),sQuery(id+"F0.wireOp",EDGE,"E16"),sQuery(id+"F0.wireOp",EDGE,"E19"),sQuery(id+"F0.wireOp",EDGE,"E20"),sQuery(id+"F0.wireOp",EDGE,"E21"),subQ0,sQuery(id+"F0.wireOp",EDGE,"E23"),sQuery(id+"F0.wireOp",EDGE,"E24"),sQuery(id+"F0.wireOp",EDGE,"E25"),sQuery(id+"F0.wireOp",EDGE,"E26"),sQuery(id+"F0.wireOp",EDGE,"E28"),sQuery(id+"F0.wireOp",EDGE,"E29"),sQuery(id+"F0.wireOp",EDGE,"E31"),sQuery(id+"F0.wireOp",EDGE,"E32"),sQuery(id+"F0.wireOp",EDGE,"E34"),sQuery(id+"F0.wireOp",EDGE,"E35"),sQuery(id+"F0.wireOp",EDGE,"E37"),sQuery(id+"F0.wireOp",EDGE,"E38")])],"isStart":true})],"blendedInto":[makeQuery(id+"F1.opExtrude","CAP_FACE",FACE,{"disambiguationData":[OSD([sQuery(id+"F0.wireOp",EDGE,"E0"),sQuery(id+"F0.wireOp",EDGE,"E2"),sQuery(id+"F0.wireOp",EDGE,"E4"),sQuery(id+"F0.wireOp",EDGE,"E6"),sQuery(id+"F0.wireOp",EDGE,"E8"),sQuery(id+"F0.wireOp",EDGE,"E10"),sQuery(id+"F0.wireOp",EDGE,"E11"),sQuery(id+"F0.wireOp",EDGE,"E14"),sQuery(id+"F0.wireOp",EDGE,"E16"),sQuery(id+"F0.wireOp",EDGE,"E19"),sQuery(id+"F0.wireOp",EDGE,"E20"),sQuery(id+"F0.wireOp",EDGE,"E21"),subQ0,sQuery(id+"F0.wireOp",EDGE,"E23"),sQuery(id+"F0.wireOp",EDGE,"E24"),sQuery(id+"F0.wireOp",EDGE,"E25"),sQuery(id+"F0.wireOp",EDGE,"E26"),sQuery(id+"F0.wireOp",EDGE,"E28"),sQuery(id+"F0.wireOp",EDGE,"E29"),sQuery(id+"F0.wireOp",EDGE,"E31"),sQuery(id+"F0.wireOp",EDGE,"E32"),sQuery(id+"F0.wireOp",EDGE,"E34"),sQuery(id+"F0.wireOp",EDGE,"E35"),sQuery(id+"F0.wireOp",EDGE,"E37"),sQuery(id+"F0.wireOp",EDGE,"E38")])],"isStart":true})]});}
            var Q8;
            {var subQ0=sQuery(id+"F0.wireOp",EDGE,"E8");Q8=makeQuery(id+"F2.opChamfer","BLEND_EDGE",EDGE,{"blendedFrom":[makeQuery(id+"F1.opExtrude","CAP_EDGE",EDGE,{"disambiguationData":[OSD([subQ0])],"isStart":false}),makeQuery(id+"F1.opExtrude","CAP_FACE",FACE,{"disambiguationData":[OSD([sQuery(id+"F0.wireOp",EDGE,"E0"),sQuery(id+"F0.wireOp",EDGE,"E2"),sQuery(id+"F0.wireOp",EDGE,"E4"),sQuery(id+"F0.wireOp",EDGE,"E6"),subQ0,sQuery(id+"F0.wireOp",EDGE,"E10"),sQuery(id+"F0.wireOp",EDGE,"E11"),sQuery(id+"F0.wireOp",EDGE,"E14"),sQuery(id+"F0.wireOp",EDGE,"E16"),sQuery(id+"F0.wireOp",EDGE,"E19"),sQuery(id+"F0.wireOp",EDGE,"E20"),sQuery(id+"F0.wireOp",EDGE,"E21"),sQuery(id+"F0.wireOp",EDGE,"E22"),sQuery(id+"F0.wireOp",EDGE,"E23"),sQuery(id+"F0.wireOp",EDGE,"E24"),sQuery(id+"F0.wireOp",EDGE,"E25"),sQuery(id+"F0.wireOp",EDGE,"E26"),sQuery(id+"F0.wireOp",EDGE,"E28"),sQuery(id+"F0.wireOp",EDGE,"E29"),sQuery(id+"F0.wireOp",EDGE,"E31"),sQuery(id+"F0.wireOp",EDGE,"E32"),sQuery(id+"F0.wireOp",EDGE,"E34"),sQuery(id+"F0.wireOp",EDGE,"E35"),sQuery(id+"F0.wireOp",EDGE,"E37"),sQuery(id+"F0.wireOp",EDGE,"E38")])],"isStart":false})],"blendedInto":[makeQuery(id+"F1.opExtrude","CAP_FACE",FACE,{"disambiguationData":[OSD([sQuery(id+"F0.wireOp",EDGE,"E0"),sQuery(id+"F0.wireOp",EDGE,"E2"),sQuery(id+"F0.wireOp",EDGE,"E4"),sQuery(id+"F0.wireOp",EDGE,"E6"),subQ0,sQuery(id+"F0.wireOp",EDGE,"E10"),sQuery(id+"F0.wireOp",EDGE,"E11"),sQuery(id+"F0.wireOp",EDGE,"E14"),sQuery(id+"F0.wireOp",EDGE,"E16"),sQuery(id+"F0.wireOp",EDGE,"E19"),sQuery(id+"F0.wireOp",EDGE,"E20"),sQuery(id+"F0.wireOp",EDGE,"E21"),sQuery(id+"F0.wireOp",EDGE,"E22"),sQuery(id+"F0.wireOp",EDGE,"E23"),sQuery(id+"F0.wireOp",EDGE,"E24"),sQuery(id+"F0.wireOp",EDGE,"E25"),sQuery(id+"F0.wireOp",EDGE,"E26"),sQuery(id+"F0.wireOp",EDGE,"E28"),sQuery(id+"F0.wireOp",EDGE,"E29"),sQuery(id+"F0.wireOp",EDGE,"E31"),sQuery(id+"F0.wireOp",EDGE,"E32"),sQuery(id+"F0.wireOp",EDGE,"E34"),sQuery(id+"F0.wireOp",EDGE,"E35"),sQuery(id+"F0.wireOp",EDGE,"E37"),sQuery(id+"F0.wireOp",EDGE,"E38")])],"isStart":false})]});}
            var Q9;
            {var subQ0=sQuery(id+"F0.wireOp",EDGE,"E24");Q9=makeQuery(id+"F2.opChamfer","BLEND_EDGE",EDGE,{"blendedFrom":[makeQuery(id+"F1.opExtrude","CAP_EDGE",EDGE,{"disambiguationData":[OSD([subQ0])],"isStart":false}),makeQuery(id+"F1.opExtrude","CAP_FACE",FACE,{"disambiguationData":[OSD([sQuery(id+"F0.wireOp",EDGE,"E0"),sQuery(id+"F0.wireOp",EDGE,"E2"),sQuery(id+"F0.wireOp",EDGE,"E4"),sQuery(id+"F0.wireOp",EDGE,"E6"),sQuery(id+"F0.wireOp",EDGE,"E8"),sQuery(id+"F0.wireOp",EDGE,"E10"),sQuery(id+"F0.wireOp",EDGE,"E11"),sQuery(id+"F0.wireOp",EDGE,"E14"),sQuery(id+"F0.wireOp",EDGE,"E16"),sQuery(id+"F0.wireOp",EDGE,"E19"),sQuery(id+"F0.wireOp",EDGE,"E20"),sQuery(id+"F0.wireOp",EDGE,"E21"),sQuery(id+"F0.wireOp",EDGE,"E22"),sQuery(id+"F0.wireOp",EDGE,"E23"),subQ0,sQuery(id+"F0.wireOp",EDGE,"E25"),sQuery(id+"F0.wireOp",EDGE,"E26"),sQuery(id+"F0.wireOp",EDGE,"E28"),sQuery(id+"F0.wireOp",EDGE,"E29"),sQuery(id+"F0.wireOp",EDGE,"E31"),sQuery(id+"F0.wireOp",EDGE,"E32"),sQuery(id+"F0.wireOp",EDGE,"E34"),sQuery(id+"F0.wireOp",EDGE,"E35"),sQuery(id+"F0.wireOp",EDGE,"E37"),sQuery(id+"F0.wireOp",EDGE,"E38")])],"isStart":false})],"blendedInto":[makeQuery(id+"F1.opExtrude","CAP_FACE",FACE,{"disambiguationData":[OSD([sQuery(id+"F0.wireOp",EDGE,"E0"),sQuery(id+"F0.wireOp",EDGE,"E2"),sQuery(id+"F0.wireOp",EDGE,"E4"),sQuery(id+"F0.wireOp",EDGE,"E6"),sQuery(id+"F0.wireOp",EDGE,"E8"),sQuery(id+"F0.wireOp",EDGE,"E10"),sQuery(id+"F0.wireOp",EDGE,"E11"),sQuery(id+"F0.wireOp",EDGE,"E14"),sQuery(id+"F0.wireOp",EDGE,"E16"),sQuery(id+"F0.wireOp",EDGE,"E19"),sQuery(id+"F0.wireOp",EDGE,"E20"),sQuery(id+"F0.wireOp",EDGE,"E21"),sQuery(id+"F0.wireOp",EDGE,"E22"),sQuery(id+"F0.wireOp",EDGE,"E23"),subQ0,sQuery(id+"F0.wireOp",EDGE,"E25"),sQuery(id+"F0.wireOp",EDGE,"E26"),sQuery(id+"F0.wireOp",EDGE,"E28"),sQuery(id+"F0.wireOp",EDGE,"E29"),sQuery(id+"F0.wireOp",EDGE,"E31"),sQuery(id+"F0.wireOp",EDGE,"E32"),sQuery(id+"F0.wireOp",EDGE,"E34"),sQuery(id+"F0.wireOp",EDGE,"E35"),sQuery(id+"F0.wireOp",EDGE,"E37"),sQuery(id+"F0.wireOp",EDGE,"E38")])],"isStart":false})]});}
            var Q10;
            {var subQ0=sQuery(id+"F0.wireOp",EDGE,"E26");Q10=makeQuery(id+"F2.opChamfer","BLEND_EDGE",EDGE,{"blendedFrom":[makeQuery(id+"F1.opExtrude","CAP_EDGE",EDGE,{"disambiguationData":[OSD([subQ0])],"isStart":false}),makeQuery(id+"F1.opExtrude","CAP_FACE",FACE,{"disambiguationData":[OSD([sQuery(id+"F0.wireOp",EDGE,"E0"),sQuery(id+"F0.wireOp",EDGE,"E2"),sQuery(id+"F0.wireOp",EDGE,"E4"),sQuery(id+"F0.wireOp",EDGE,"E6"),sQuery(id+"F0.wireOp",EDGE,"E8"),sQuery(id+"F0.wireOp",EDGE,"E10"),sQuery(id+"F0.wireOp",EDGE,"E11"),sQuery(id+"F0.wireOp",EDGE,"E14"),sQuery(id+"F0.wireOp",EDGE,"E16"),sQuery(id+"F0.wireOp",EDGE,"E19"),sQuery(id+"F0.wireOp",EDGE,"E20"),sQuery(id+"F0.wireOp",EDGE,"E21"),sQuery(id+"F0.wireOp",EDGE,"E22"),sQuery(id+"F0.wireOp",EDGE,"E23"),sQuery(id+"F0.wireOp",EDGE,"E24"),sQuery(id+"F0.wireOp",EDGE,"E25"),subQ0,sQuery(id+"F0.wireOp",EDGE,"E28"),sQuery(id+"F0.wireOp",EDGE,"E29"),sQuery(id+"F0.wireOp",EDGE,"E31"),sQuery(id+"F0.wireOp",EDGE,"E32"),sQuery(id+"F0.wireOp",EDGE,"E34"),sQuery(id+"F0.wireOp",EDGE,"E35"),sQuery(id+"F0.wireOp",EDGE,"E37"),sQuery(id+"F0.wireOp",EDGE,"E38")])],"isStart":false})],"blendedInto":[makeQuery(id+"F1.opExtrude","CAP_FACE",FACE,{"disambiguationData":[OSD([sQuery(id+"F0.wireOp",EDGE,"E0"),sQuery(id+"F0.wireOp",EDGE,"E2"),sQuery(id+"F0.wireOp",EDGE,"E4"),sQuery(id+"F0.wireOp",EDGE,"E6"),sQuery(id+"F0.wireOp",EDGE,"E8"),sQuery(id+"F0.wireOp",EDGE,"E10"),sQuery(id+"F0.wireOp",EDGE,"E11"),sQuery(id+"F0.wireOp",EDGE,"E14"),sQuery(id+"F0.wireOp",EDGE,"E16"),sQuery(id+"F0.wireOp",EDGE,"E19"),sQuery(id+"F0.wireOp",EDGE,"E20"),sQuery(id+"F0.wireOp",EDGE,"E21"),sQuery(id+"F0.wireOp",EDGE,"E22"),sQuery(id+"F0.wireOp",EDGE,"E23"),sQuery(id+"F0.wireOp",EDGE,"E24"),sQuery(id+"F0.wireOp",EDGE,"E25"),subQ0,sQuery(id+"F0.wireOp",EDGE,"E28"),sQuery(id+"F0.wireOp",EDGE,"E29"),sQuery(id+"F0.wireOp",EDGE,"E31"),sQuery(id+"F0.wireOp",EDGE,"E32"),sQuery(id+"F0.wireOp",EDGE,"E34"),sQuery(id+"F0.wireOp",EDGE,"E35"),sQuery(id+"F0.wireOp",EDGE,"E37"),sQuery(id+"F0.wireOp",EDGE,"E38")])],"isStart":false})]});}
            var Q11;
            {var subQ0=sQuery(id+"F0.wireOp",EDGE,"E4");Q11=makeQuery(id+"F2.opChamfer","BLEND_EDGE",EDGE,{"blendedFrom":[makeQuery(id+"F1.opExtrude","CAP_EDGE",EDGE,{"disambiguationData":[OSD([subQ0])],"isStart":false}),makeQuery(id+"F1.opExtrude","CAP_FACE",FACE,{"disambiguationData":[OSD([sQuery(id+"F0.wireOp",EDGE,"E0"),sQuery(id+"F0.wireOp",EDGE,"E2"),subQ0,sQuery(id+"F0.wireOp",EDGE,"E6"),sQuery(id+"F0.wireOp",EDGE,"E8"),sQuery(id+"F0.wireOp",EDGE,"E10"),sQuery(id+"F0.wireOp",EDGE,"E11"),sQuery(id+"F0.wireOp",EDGE,"E14"),sQuery(id+"F0.wireOp",EDGE,"E16"),sQuery(id+"F0.wireOp",EDGE,"E19"),sQuery(id+"F0.wireOp",EDGE,"E20"),sQuery(id+"F0.wireOp",EDGE,"E21"),sQuery(id+"F0.wireOp",EDGE,"E22"),sQuery(id+"F0.wireOp",EDGE,"E23"),sQuery(id+"F0.wireOp",EDGE,"E24"),sQuery(id+"F0.wireOp",EDGE,"E25"),sQuery(id+"F0.wireOp",EDGE,"E26"),sQuery(id+"F0.wireOp",EDGE,"E28"),sQuery(id+"F0.wireOp",EDGE,"E29"),sQuery(id+"F0.wireOp",EDGE,"E31"),sQuery(id+"F0.wireOp",EDGE,"E32"),sQuery(id+"F0.wireOp",EDGE,"E34"),sQuery(id+"F0.wireOp",EDGE,"E35"),sQuery(id+"F0.wireOp",EDGE,"E37"),sQuery(id+"F0.wireOp",EDGE,"E38")])],"isStart":false})],"blendedInto":[makeQuery(id+"F1.opExtrude","CAP_FACE",FACE,{"disambiguationData":[OSD([sQuery(id+"F0.wireOp",EDGE,"E0"),sQuery(id+"F0.wireOp",EDGE,"E2"),subQ0,sQuery(id+"F0.wireOp",EDGE,"E6"),sQuery(id+"F0.wireOp",EDGE,"E8"),sQuery(id+"F0.wireOp",EDGE,"E10"),sQuery(id+"F0.wireOp",EDGE,"E11"),sQuery(id+"F0.wireOp",EDGE,"E14"),sQuery(id+"F0.wireOp",EDGE,"E16"),sQuery(id+"F0.wireOp",EDGE,"E19"),sQuery(id+"F0.wireOp",EDGE,"E20"),sQuery(id+"F0.wireOp",EDGE,"E21"),sQuery(id+"F0.wireOp",EDGE,"E22"),sQuery(id+"F0.wireOp",EDGE,"E23"),sQuery(id+"F0.wireOp",EDGE,"E24"),sQuery(id+"F0.wireOp",EDGE,"E25"),sQuery(id+"F0.wireOp",EDGE,"E26"),sQuery(id+"F0.wireOp",EDGE,"E28"),sQuery(id+"F0.wireOp",EDGE,"E29"),sQuery(id+"F0.wireOp",EDGE,"E31"),sQuery(id+"F0.wireOp",EDGE,"E32"),sQuery(id+"F0.wireOp",EDGE,"E34"),sQuery(id+"F0.wireOp",EDGE,"E35"),sQuery(id+"F0.wireOp",EDGE,"E37"),sQuery(id+"F0.wireOp",EDGE,"E38")])],"isStart":false})]});}
            var Q12;
            {var subQ0=sQuery(id+"F0.wireOp",EDGE,"E11");Q12=makeQuery(id+"F2.opChamfer","BLEND_EDGE",EDGE,{"blendedFrom":[makeQuery(id+"F1.opExtrude","CAP_EDGE",EDGE,{"disambiguationData":[OSD([subQ0])],"isStart":false}),makeQuery(id+"F1.opExtrude","CAP_FACE",FACE,{"disambiguationData":[OSD([sQuery(id+"F0.wireOp",EDGE,"E0"),sQuery(id+"F0.wireOp",EDGE,"E2"),sQuery(id+"F0.wireOp",EDGE,"E4"),sQuery(id+"F0.wireOp",EDGE,"E6"),sQuery(id+"F0.wireOp",EDGE,"E8"),sQuery(id+"F0.wireOp",EDGE,"E10"),subQ0,sQuery(id+"F0.wireOp",EDGE,"E14"),sQuery(id+"F0.wireOp",EDGE,"E16"),sQuery(id+"F0.wireOp",EDGE,"E19"),sQuery(id+"F0.wireOp",EDGE,"E20"),sQuery(id+"F0.wireOp",EDGE,"E21"),sQuery(id+"F0.wireOp",EDGE,"E22"),sQuery(id+"F0.wireOp",EDGE,"E23"),sQuery(id+"F0.wireOp",EDGE,"E24"),sQuery(id+"F0.wireOp",EDGE,"E25"),sQuery(id+"F0.wireOp",EDGE,"E26"),sQuery(id+"F0.wireOp",EDGE,"E28"),sQuery(id+"F0.wireOp",EDGE,"E29"),sQuery(id+"F0.wireOp",EDGE,"E31"),sQuery(id+"F0.wireOp",EDGE,"E32"),sQuery(id+"F0.wireOp",EDGE,"E34"),sQuery(id+"F0.wireOp",EDGE,"E35"),sQuery(id+"F0.wireOp",EDGE,"E37"),sQuery(id+"F0.wireOp",EDGE,"E38")])],"isStart":false})],"blendedInto":[makeQuery(id+"F1.opExtrude","CAP_FACE",FACE,{"disambiguationData":[OSD([sQuery(id+"F0.wireOp",EDGE,"E0"),sQuery(id+"F0.wireOp",EDGE,"E2"),sQuery(id+"F0.wireOp",EDGE,"E4"),sQuery(id+"F0.wireOp",EDGE,"E6"),sQuery(id+"F0.wireOp",EDGE,"E8"),sQuery(id+"F0.wireOp",EDGE,"E10"),subQ0,sQuery(id+"F0.wireOp",EDGE,"E14"),sQuery(id+"F0.wireOp",EDGE,"E16"),sQuery(id+"F0.wireOp",EDGE,"E19"),sQuery(id+"F0.wireOp",EDGE,"E20"),sQuery(id+"F0.wireOp",EDGE,"E21"),sQuery(id+"F0.wireOp",EDGE,"E22"),sQuery(id+"F0.wireOp",EDGE,"E23"),sQuery(id+"F0.wireOp",EDGE,"E24"),sQuery(id+"F0.wireOp",EDGE,"E25"),sQuery(id+"F0.wireOp",EDGE,"E26"),sQuery(id+"F0.wireOp",EDGE,"E28"),sQuery(id+"F0.wireOp",EDGE,"E29"),sQuery(id+"F0.wireOp",EDGE,"E31"),sQuery(id+"F0.wireOp",EDGE,"E32"),sQuery(id+"F0.wireOp",EDGE,"E34"),sQuery(id+"F0.wireOp",EDGE,"E35"),sQuery(id+"F0.wireOp",EDGE,"E37"),sQuery(id+"F0.wireOp",EDGE,"E38")])],"isStart":false})]});}
            var Q13;
            {var subQ0=sQuery(id+"F0.wireOp",EDGE,"E22");Q13=makeQuery(id+"F2.opChamfer","BLEND_EDGE",EDGE,{"blendedFrom":[makeQuery(id+"F1.opExtrude","CAP_EDGE",EDGE,{"disambiguationData":[OSD([subQ0])],"isStart":false}),makeQuery(id+"F1.opExtrude","CAP_FACE",FACE,{"disambiguationData":[OSD([sQuery(id+"F0.wireOp",EDGE,"E0"),sQuery(id+"F0.wireOp",EDGE,"E2"),sQuery(id+"F0.wireOp",EDGE,"E4"),sQuery(id+"F0.wireOp",EDGE,"E6"),sQuery(id+"F0.wireOp",EDGE,"E8"),sQuery(id+"F0.wireOp",EDGE,"E10"),sQuery(id+"F0.wireOp",EDGE,"E11"),sQuery(id+"F0.wireOp",EDGE,"E14"),sQuery(id+"F0.wireOp",EDGE,"E16"),sQuery(id+"F0.wireOp",EDGE,"E19"),sQuery(id+"F0.wireOp",EDGE,"E20"),sQuery(id+"F0.wireOp",EDGE,"E21"),subQ0,sQuery(id+"F0.wireOp",EDGE,"E23"),sQuery(id+"F0.wireOp",EDGE,"E24"),sQuery(id+"F0.wireOp",EDGE,"E25"),sQuery(id+"F0.wireOp",EDGE,"E26"),sQuery(id+"F0.wireOp",EDGE,"E28"),sQuery(id+"F0.wireOp",EDGE,"E29"),sQuery(id+"F0.wireOp",EDGE,"E31"),sQuery(id+"F0.wireOp",EDGE,"E32"),sQuery(id+"F0.wireOp",EDGE,"E34"),sQuery(id+"F0.wireOp",EDGE,"E35"),sQuery(id+"F0.wireOp",EDGE,"E37"),sQuery(id+"F0.wireOp",EDGE,"E38")])],"isStart":false})],"blendedInto":[makeQuery(id+"F1.opExtrude","CAP_FACE",FACE,{"disambiguationData":[OSD([sQuery(id+"F0.wireOp",EDGE,"E0"),sQuery(id+"F0.wireOp",EDGE,"E2"),sQuery(id+"F0.wireOp",EDGE,"E4"),sQuery(id+"F0.wireOp",EDGE,"E6"),sQuery(id+"F0.wireOp",EDGE,"E8"),sQuery(id+"F0.wireOp",EDGE,"E10"),sQuery(id+"F0.wireOp",EDGE,"E11"),sQuery(id+"F0.wireOp",EDGE,"E14"),sQuery(id+"F0.wireOp",EDGE,"E16"),sQuery(id+"F0.wireOp",EDGE,"E19"),sQuery(id+"F0.wireOp",EDGE,"E20"),sQuery(id+"F0.wireOp",EDGE,"E21"),subQ0,sQuery(id+"F0.wireOp",EDGE,"E23"),sQuery(id+"F0.wireOp",EDGE,"E24"),sQuery(id+"F0.wireOp",EDGE,"E25"),sQuery(id+"F0.wireOp",EDGE,"E26"),sQuery(id+"F0.wireOp",EDGE,"E28"),sQuery(id+"F0.wireOp",EDGE,"E29"),sQuery(id+"F0.wireOp",EDGE,"E31"),sQuery(id+"F0.wireOp",EDGE,"E32"),sQuery(id+"F0.wireOp",EDGE,"E34"),sQuery(id+"F0.wireOp",EDGE,"E35"),sQuery(id+"F0.wireOp",EDGE,"E37"),sQuery(id+"F0.wireOp",EDGE,"E38")])],"isStart":false})]});}
            var Q14;
            {var subQ0=sQuery(id+"F0.wireOp",EDGE,"E20");Q14=makeQuery(id+"F2.opChamfer","BLEND_EDGE",EDGE,{"blendedFrom":[makeQuery(id+"F1.opExtrude","CAP_EDGE",EDGE,{"disambiguationData":[OSD([subQ0])],"isStart":false}),makeQuery(id+"F1.opExtrude","CAP_FACE",FACE,{"disambiguationData":[OSD([sQuery(id+"F0.wireOp",EDGE,"E0"),sQuery(id+"F0.wireOp",EDGE,"E2"),sQuery(id+"F0.wireOp",EDGE,"E4"),sQuery(id+"F0.wireOp",EDGE,"E6"),sQuery(id+"F0.wireOp",EDGE,"E8"),sQuery(id+"F0.wireOp",EDGE,"E10"),sQuery(id+"F0.wireOp",EDGE,"E11"),sQuery(id+"F0.wireOp",EDGE,"E14"),sQuery(id+"F0.wireOp",EDGE,"E16"),sQuery(id+"F0.wireOp",EDGE,"E19"),subQ0,sQuery(id+"F0.wireOp",EDGE,"E21"),sQuery(id+"F0.wireOp",EDGE,"E22"),sQuery(id+"F0.wireOp",EDGE,"E23"),sQuery(id+"F0.wireOp",EDGE,"E24"),sQuery(id+"F0.wireOp",EDGE,"E25"),sQuery(id+"F0.wireOp",EDGE,"E26"),sQuery(id+"F0.wireOp",EDGE,"E28"),sQuery(id+"F0.wireOp",EDGE,"E29"),sQuery(id+"F0.wireOp",EDGE,"E31"),sQuery(id+"F0.wireOp",EDGE,"E32"),sQuery(id+"F0.wireOp",EDGE,"E34"),sQuery(id+"F0.wireOp",EDGE,"E35"),sQuery(id+"F0.wireOp",EDGE,"E37"),sQuery(id+"F0.wireOp",EDGE,"E38")])],"isStart":false})],"blendedInto":[makeQuery(id+"F1.opExtrude","CAP_FACE",FACE,{"disambiguationData":[OSD([sQuery(id+"F0.wireOp",EDGE,"E0"),sQuery(id+"F0.wireOp",EDGE,"E2"),sQuery(id+"F0.wireOp",EDGE,"E4"),sQuery(id+"F0.wireOp",EDGE,"E6"),sQuery(id+"F0.wireOp",EDGE,"E8"),sQuery(id+"F0.wireOp",EDGE,"E10"),sQuery(id+"F0.wireOp",EDGE,"E11"),sQuery(id+"F0.wireOp",EDGE,"E14"),sQuery(id+"F0.wireOp",EDGE,"E16"),sQuery(id+"F0.wireOp",EDGE,"E19"),subQ0,sQuery(id+"F0.wireOp",EDGE,"E21"),sQuery(id+"F0.wireOp",EDGE,"E22"),sQuery(id+"F0.wireOp",EDGE,"E23"),sQuery(id+"F0.wireOp",EDGE,"E24"),sQuery(id+"F0.wireOp",EDGE,"E25"),sQuery(id+"F0.wireOp",EDGE,"E26"),sQuery(id+"F0.wireOp",EDGE,"E28"),sQuery(id+"F0.wireOp",EDGE,"E29"),sQuery(id+"F0.wireOp",EDGE,"E31"),sQuery(id+"F0.wireOp",EDGE,"E32"),sQuery(id+"F0.wireOp",EDGE,"E34"),sQuery(id+"F0.wireOp",EDGE,"E35"),sQuery(id+"F0.wireOp",EDGE,"E37"),sQuery(id+"F0.wireOp",EDGE,"E38")])],"isStart":false})]});}
            var Q15;
            {var subQ0=sQuery(id+"F0.wireOp",EDGE,"E16");Q15=makeQuery(id+"F2.opChamfer","BLEND_EDGE",EDGE,{"blendedFrom":[makeQuery(id+"F1.opExtrude","CAP_EDGE",EDGE,{"disambiguationData":[OSD([subQ0])],"isStart":false}),makeQuery(id+"F1.opExtrude","CAP_FACE",FACE,{"disambiguationData":[OSD([sQuery(id+"F0.wireOp",EDGE,"E0"),sQuery(id+"F0.wireOp",EDGE,"E2"),sQuery(id+"F0.wireOp",EDGE,"E4"),sQuery(id+"F0.wireOp",EDGE,"E6"),sQuery(id+"F0.wireOp",EDGE,"E8"),sQuery(id+"F0.wireOp",EDGE,"E10"),sQuery(id+"F0.wireOp",EDGE,"E11"),sQuery(id+"F0.wireOp",EDGE,"E14"),subQ0,sQuery(id+"F0.wireOp",EDGE,"E19"),sQuery(id+"F0.wireOp",EDGE,"E20"),sQuery(id+"F0.wireOp",EDGE,"E21"),sQuery(id+"F0.wireOp",EDGE,"E22"),sQuery(id+"F0.wireOp",EDGE,"E23"),sQuery(id+"F0.wireOp",EDGE,"E24"),sQuery(id+"F0.wireOp",EDGE,"E25"),sQuery(id+"F0.wireOp",EDGE,"E26"),sQuery(id+"F0.wireOp",EDGE,"E28"),sQuery(id+"F0.wireOp",EDGE,"E29"),sQuery(id+"F0.wireOp",EDGE,"E31"),sQuery(id+"F0.wireOp",EDGE,"E32"),sQuery(id+"F0.wireOp",EDGE,"E34"),sQuery(id+"F0.wireOp",EDGE,"E35"),sQuery(id+"F0.wireOp",EDGE,"E37"),sQuery(id+"F0.wireOp",EDGE,"E38")])],"isStart":false})],"blendedInto":[makeQuery(id+"F1.opExtrude","CAP_FACE",FACE,{"disambiguationData":[OSD([sQuery(id+"F0.wireOp",EDGE,"E0"),sQuery(id+"F0.wireOp",EDGE,"E2"),sQuery(id+"F0.wireOp",EDGE,"E4"),sQuery(id+"F0.wireOp",EDGE,"E6"),sQuery(id+"F0.wireOp",EDGE,"E8"),sQuery(id+"F0.wireOp",EDGE,"E10"),sQuery(id+"F0.wireOp",EDGE,"E11"),sQuery(id+"F0.wireOp",EDGE,"E14"),subQ0,sQuery(id+"F0.wireOp",EDGE,"E19"),sQuery(id+"F0.wireOp",EDGE,"E20"),sQuery(id+"F0.wireOp",EDGE,"E21"),sQuery(id+"F0.wireOp",EDGE,"E22"),sQuery(id+"F0.wireOp",EDGE,"E23"),sQuery(id+"F0.wireOp",EDGE,"E24"),sQuery(id+"F0.wireOp",EDGE,"E25"),sQuery(id+"F0.wireOp",EDGE,"E26"),sQuery(id+"F0.wireOp",EDGE,"E28"),sQuery(id+"F0.wireOp",EDGE,"E29"),sQuery(id+"F0.wireOp",EDGE,"E31"),sQuery(id+"F0.wireOp",EDGE,"E32"),sQuery(id+"F0.wireOp",EDGE,"E34"),sQuery(id+"F0.wireOp",EDGE,"E35"),sQuery(id+"F0.wireOp",EDGE,"E37"),sQuery(id+"F0.wireOp",EDGE,"E38")])],"isStart":false})]});}
            chamfer(context, id + "F3", {"entities" : qUnion([Q0, Q1, Q2, Q3, Q4, Q5, Q6, Q7, Q8, Q9, Q10, Q11, Q12, Q13, Q14, Q15]), "width" : 3 * mm, "tangentPropagation" : true});
        }
    });
